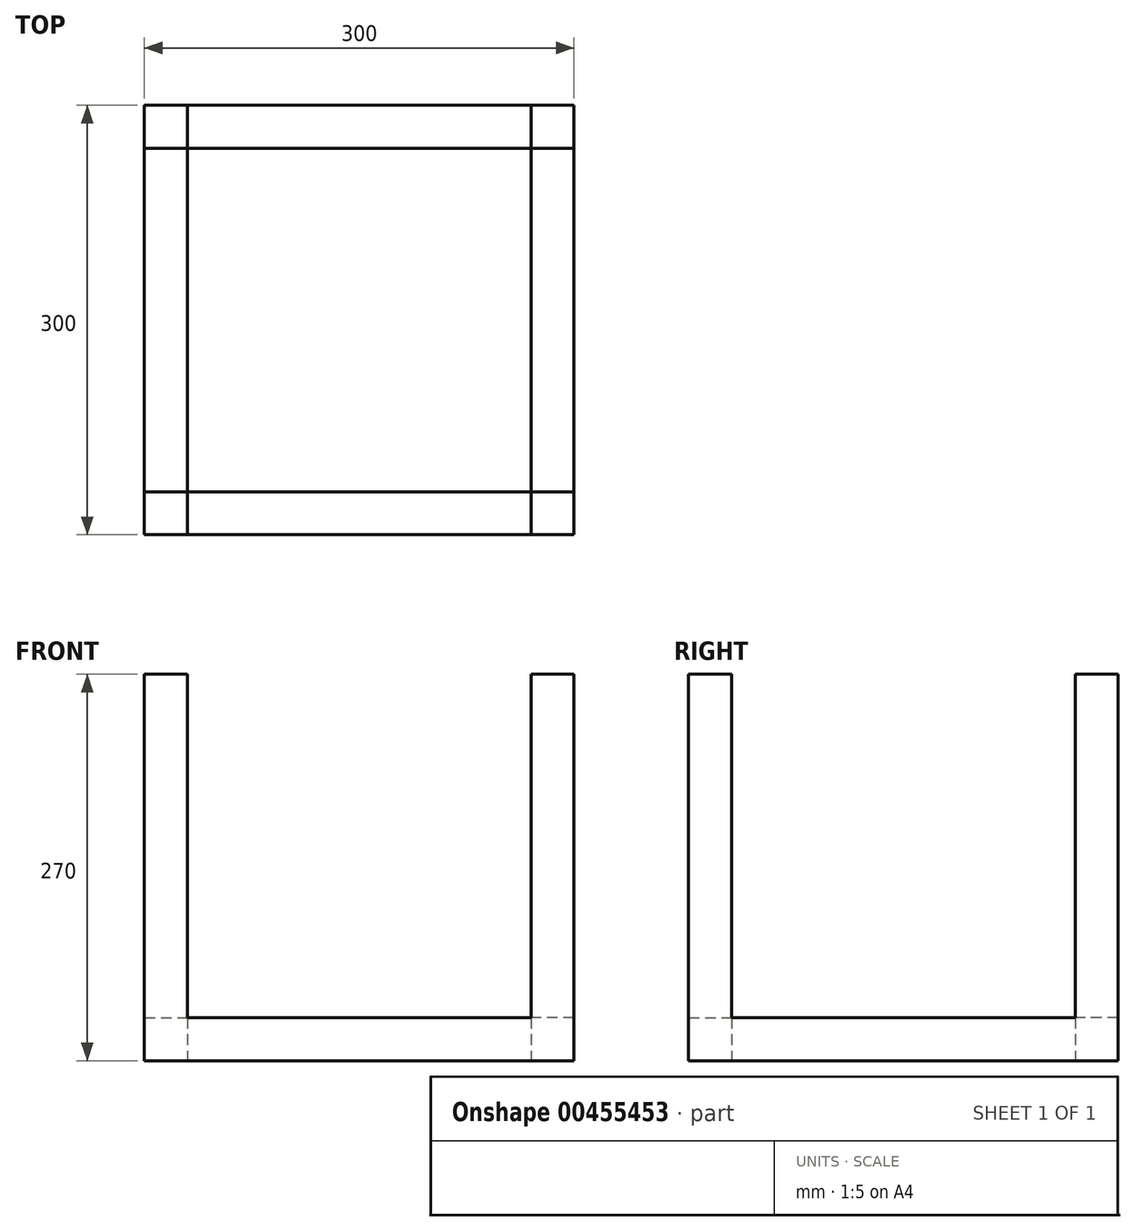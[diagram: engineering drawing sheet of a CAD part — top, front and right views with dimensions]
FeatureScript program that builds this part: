
annotation { "Feature Type Name" : "Feature", "Feature Type Description" : "" }
export const myFeature = defineFeature(function(context is Context, id is Id, definition is map)
    precondition{}
    {
        {
            var Q0;
            Q0=qCreatedBy(makeId("Top.planeOp"),FACE);
            var sketch = newSketch(context, id + "F0", { "sketchPlane" : qUnion([Q0])});
            skLineSegment(sketch, "E0.bottom", {"start": v(150, -150) * mm, "end": v(-150, -150) * mm});
            skLineSegment(sketch, "E0.top", {"start": v(150, 150) * mm, "end": v(-150, 150) * mm});
            skLineSegment(sketch, "E0.left", {"start": v(150, -150) * mm, "end": v(150, 150) * mm});
            skLineSegment(sketch, "E0.right", {"start": v(-150, -150) * mm, "end": v(-150, 150) * mm});
            skPoint(sketch, "E0.middle", {"position": v(0, 0) * mm});
            skLineSegment(sketch, "E1.0", {"start": v(120, -120) * mm, "end": v(120, 120) * mm});
            skLineSegment(sketch, "E1.1", {"start": v(120, -120) * mm, "end": v(-120, -120) * mm});
            skLineSegment(sketch, "E1.2", {"start": v(-120, -120) * mm, "end": v(-120, 120) * mm});
            skLineSegment(sketch, "E1.3", {"start": v(120, 120) * mm, "end": v(-120, 120) * mm});
            skSolve(sketch);
        }
        {
            var Q0;
            Q0 = qSketchRegion(id + "F0", true);
            extrude(context, id + "F1", {"entities" : qUnion([Q0]), "depth" : 30 * mm});
        }
        {
            var Q0;
            Q0=makeQuery(id+"F1.opExtrude","CAP_FACE",FACE,{"disambiguationData":[OSD([sQuery(id+"F0.wireOp",EDGE,"E0.bottom"),sQuery(id+"F0.wireOp",EDGE,"E0.top"),sQuery(id+"F0.wireOp",EDGE,"E0.left"),sQuery(id+"F0.wireOp",EDGE,"E0.right"),sQuery(id+"F0.wireOp",EDGE,"E1.0"),sQuery(id+"F0.wireOp",EDGE,"E1.1"),sQuery(id+"F0.wireOp",EDGE,"E1.2"),sQuery(id+"F0.wireOp",EDGE,"E1.3")])],"isStart":false});
            var sketch = newSketch(context, id + "F2", { "sketchPlane" : qUnion([Q0])});
            skLineSegment(sketch, "E2.bottom", {"start": v(-150, -150) * mm, "end": v(-120, -150) * mm});
            skLineSegment(sketch, "E2.top", {"start": v(-150, -120) * mm, "end": v(-120, -120) * mm});
            skLineSegment(sketch, "E2.left", {"start": v(-150, -150) * mm, "end": v(-150, -120) * mm});
            skLineSegment(sketch, "E2.right", {"start": v(-120, -150) * mm, "end": v(-120, -120) * mm});
            skLineSegment(sketch, "E3.bottom", {"start": v(-150, 150) * mm, "end": v(-120, 150) * mm});
            skLineSegment(sketch, "E3.top", {"start": v(-150, 120) * mm, "end": v(-120, 120) * mm});
            skLineSegment(sketch, "E3.left", {"start": v(-150, 150) * mm, "end": v(-150, 120) * mm});
            skLineSegment(sketch, "E3.right", {"start": v(-120, 150) * mm, "end": v(-120, 120) * mm});
            skLineSegment(sketch, "E4.bottom", {"start": v(150, 150) * mm, "end": v(120, 150) * mm});
            skLineSegment(sketch, "E4.top", {"start": v(150, 120) * mm, "end": v(120, 120) * mm});
            skLineSegment(sketch, "E4.left", {"start": v(150, 150) * mm, "end": v(150, 120) * mm});
            skLineSegment(sketch, "E4.right", {"start": v(120, 150) * mm, "end": v(120, 120) * mm});
            skLineSegment(sketch, "E5.bottom", {"start": v(150, -150) * mm, "end": v(120, -150) * mm});
            skLineSegment(sketch, "E5.top", {"start": v(150, -120) * mm, "end": v(120, -120) * mm});
            skLineSegment(sketch, "E5.left", {"start": v(150, -150) * mm, "end": v(150, -120) * mm});
            skLineSegment(sketch, "E5.right", {"start": v(120, -150) * mm, "end": v(120, -120) * mm});
            skSolve(sketch);
        }
        {
            var Q0;
            Q0=makeQuery(id+"F2.imprint","IMPRINT",FACE,{"disambiguationData":[TD([[makeQuery(id+"F2.imprint","IMPRINT",EDGE,{"derivedFrom":sQuery(id+"F2.wireOp",EDGE,"E3.bottom")}),1.0]])]});
            var Q1;
            Q1=makeQuery(id+"F2.imprint","IMPRINT",FACE,{"disambiguationData":[TD([[makeQuery(id+"F2.imprint","IMPRINT",EDGE,{"derivedFrom":sQuery(id+"F2.wireOp",EDGE,"E4.bottom")}),1.0]])]});
            var Q2;
            Q2=makeQuery(id+"F2.imprint","IMPRINT",FACE,{"disambiguationData":[TD([[makeQuery(id+"F2.imprint","IMPRINT",EDGE,{"derivedFrom":sQuery(id+"F2.wireOp",EDGE,"E5.bottom")}),-1.0]])]});
            var Q3;
            Q3=makeQuery(id+"F2.imprint","IMPRINT",FACE,{"disambiguationData":[TD([[makeQuery(id+"F2.imprint","IMPRINT",EDGE,{"derivedFrom":sQuery(id+"F2.wireOp",EDGE,"E2.bottom")}),-1.0]])]});
            extrude(context, id + "F3", {"entities" : qUnion([Q0, Q1, Q2, Q3]), "operationType" : NewBodyOperationType.ADD, "depth" : 240 * mm});
        }
    });
